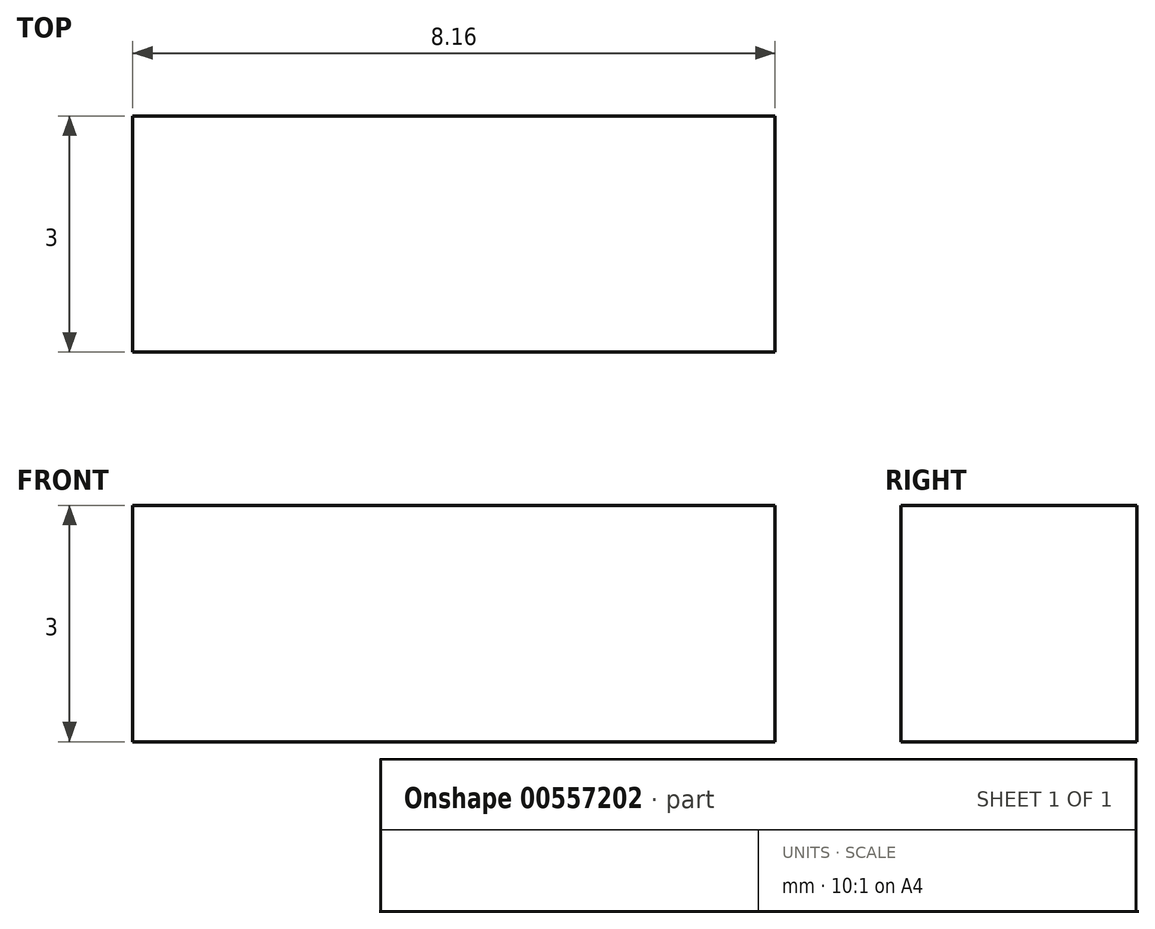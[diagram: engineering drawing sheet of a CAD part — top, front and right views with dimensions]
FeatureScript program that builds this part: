
annotation { "Feature Type Name" : "Feature", "Feature Type Description" : "" }
export const myFeature = defineFeature(function(context is Context, id is Id, definition is map)
    precondition{}
    {
        {
            var Q0;
            Q0=qCreatedBy(makeId("Top.planeOp"),FACE);
            var sketch = newSketch(context, id + "F0", { "sketchPlane" : qUnion([Q0])});
            skLineSegment(sketch, "E0.bottom", {"start": v(-6.58, -3.4) * mm, "end": v(1.58, -3.4) * mm});
            skLineSegment(sketch, "E0.top", {"start": v(-6.58, -0.4) * mm, "end": v(1.58, -0.4) * mm});
            skLineSegment(sketch, "E0.left", {"start": v(-6.58, -3.4) * mm, "end": v(-6.58, -0.4) * mm});
            skLineSegment(sketch, "E0.right", {"start": v(1.58, -3.4) * mm, "end": v(1.58, -0.4) * mm});
            skSolve(sketch);
        }
        {
            var Q0;
            Q0=makeQuery(id+"F0.imprint","IMPRINT",FACE,{"disambiguationData":[TD([[makeQuery(id+"F0.imprint","IMPRINT",EDGE,{"derivedFrom":sQuery(id+"F0.wireOp",EDGE,"E0.bottom")}),1.0]])]});
            extrude(context, id + "F1", {"entities" : qUnion([Q0]), "depth" : 3 * mm, "offsetDistance" : 25 * mm});
        }
    });
